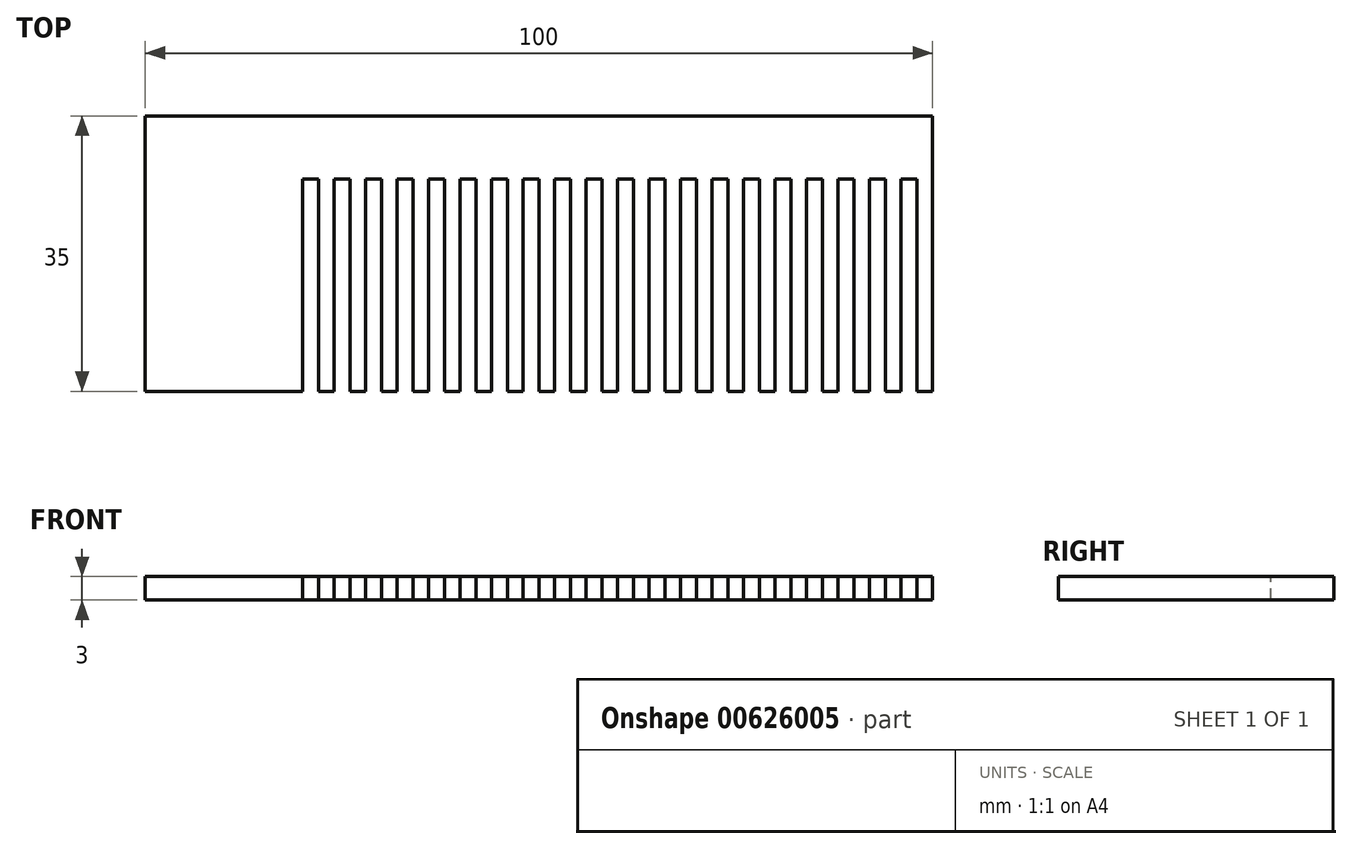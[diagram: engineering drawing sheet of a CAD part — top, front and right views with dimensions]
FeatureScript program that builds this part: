
annotation { "Feature Type Name" : "Feature", "Feature Type Description" : "" }
export const myFeature = defineFeature(function(context is Context, id is Id, definition is map)
    precondition{}
    {
        {
            var Q0;
            Q0=qCreatedBy(makeId("Top.planeOp"),FACE);
            var sketch = newSketch(context, id + "F0", { "sketchPlane" : qUnion([Q0])});
            skLineSegment(sketch, "E0.bottom", {"start": v(-50, 17.5) * mm, "end": v(50, 17.5) * mm});
            skLineSegment(sketch, "E0.top", {"start": v(-50, -17.5) * mm, "end": v(50, -17.5) * mm});
            skLineSegment(sketch, "E0.left", {"start": v(-50, 17.5) * mm, "end": v(-50, -17.5) * mm});
            skLineSegment(sketch, "E0.right", {"start": v(50, 17.5) * mm, "end": v(50, -17.5) * mm});
            skPoint(sketch, "E0.middle", {"position": v(0, 0) * mm});
            skSolve(sketch);
        }
        {
            var Q0;
            Q0=makeQuery(id+"F0.imprint","IMPRINT",FACE,{"disambiguationData":[TD([[makeQuery(id+"F0.imprint","IMPRINT",EDGE,{"derivedFrom":sQuery(id+"F0.wireOp",EDGE,"E0.bottom")}),-1.0]])]});
            extrude(context, id + "F1", {"entities" : qUnion([Q0]), "depth" : 3 * mm, "offsetDistance" : 25.4 * mm});
        }
        {
            var Q0;
            Q0=makeQuery(id+"F1.opExtrude","CAP_FACE",FACE,{"disambiguationData":[OSD([sQuery(id+"F0.wireOp",EDGE,"E0.bottom"),sQuery(id+"F0.wireOp",EDGE,"E0.top"),sQuery(id+"F0.wireOp",EDGE,"E0.left"),sQuery(id+"F0.wireOp",EDGE,"E0.right")])],"isStart":false});
            var sketch = newSketch(context, id + "F2", { "sketchPlane" : qUnion([Q0])});
            skLineSegment(sketch, "E1.bottom", {"start": v(46, 9.5) * mm, "end": v(48, 9.5) * mm});
            skLineSegment(sketch, "E1.top", {"start": v(46, -25.5) * mm, "end": v(48, -25.5) * mm});
            skLineSegment(sketch, "E1.left", {"start": v(46, 9.5) * mm, "end": v(46, -25.5) * mm});
            skLineSegment(sketch, "E1.right", {"start": v(48, 9.5) * mm, "end": v(48, -25.5) * mm});
            skLineSegment(sketch, "E2.1.0.0", {"start": v(42, 9.5) * mm, "end": v(44, 9.5) * mm});
            skLineSegment(sketch, "E2.1.0.1", {"start": v(42, -25.5) * mm, "end": v(44, -25.5) * mm});
            skLineSegment(sketch, "E2.1.0.2", {"start": v(42, 9.5) * mm, "end": v(42, -25.5) * mm});
            skLineSegment(sketch, "E2.1.0.3", {"start": v(44, 9.5) * mm, "end": v(44, -25.5) * mm});
            skLineSegment(sketch, "E2.2.0.0", {"start": v(38, 9.5) * mm, "end": v(40, 9.5) * mm});
            skLineSegment(sketch, "E2.2.0.1", {"start": v(38, -25.5) * mm, "end": v(40, -25.5) * mm});
            skLineSegment(sketch, "E2.2.0.2", {"start": v(38, 9.5) * mm, "end": v(38, -25.5) * mm});
            skLineSegment(sketch, "E2.2.0.3", {"start": v(40, 9.5) * mm, "end": v(40, -25.5) * mm});
            skLineSegment(sketch, "E2.3.0.0", {"start": v(34, 9.5) * mm, "end": v(36, 9.5) * mm});
            skLineSegment(sketch, "E2.3.0.1", {"start": v(34, -25.5) * mm, "end": v(36, -25.5) * mm});
            skLineSegment(sketch, "E2.3.0.2", {"start": v(34, 9.5) * mm, "end": v(34, -25.5) * mm});
            skLineSegment(sketch, "E2.3.0.3", {"start": v(36, 9.5) * mm, "end": v(36, -25.5) * mm});
            skLineSegment(sketch, "E2.4.0.0", {"start": v(30, 9.5) * mm, "end": v(32, 9.5) * mm});
            skLineSegment(sketch, "E2.4.0.1", {"start": v(30, -25.5) * mm, "end": v(32, -25.5) * mm});
            skLineSegment(sketch, "E2.4.0.2", {"start": v(30, 9.5) * mm, "end": v(30, -25.5) * mm});
            skLineSegment(sketch, "E2.4.0.3", {"start": v(32, 9.5) * mm, "end": v(32, -25.5) * mm});
            skLineSegment(sketch, "E2.5.0.0", {"start": v(26, 9.5) * mm, "end": v(28, 9.5) * mm});
            skLineSegment(sketch, "E2.5.0.1", {"start": v(26, -25.5) * mm, "end": v(28, -25.5) * mm});
            skLineSegment(sketch, "E2.5.0.2", {"start": v(26, 9.5) * mm, "end": v(26, -25.5) * mm});
            skLineSegment(sketch, "E2.5.0.3", {"start": v(28, 9.5) * mm, "end": v(28, -25.5) * mm});
            skLineSegment(sketch, "E2.6.0.0", {"start": v(22, 9.5) * mm, "end": v(24, 9.5) * mm});
            skLineSegment(sketch, "E2.6.0.1", {"start": v(22, -25.5) * mm, "end": v(24, -25.5) * mm});
            skLineSegment(sketch, "E2.6.0.2", {"start": v(22, 9.5) * mm, "end": v(22, -25.5) * mm});
            skLineSegment(sketch, "E2.6.0.3", {"start": v(24, 9.5) * mm, "end": v(24, -25.5) * mm});
            skLineSegment(sketch, "E2.7.0.0", {"start": v(18, 9.5) * mm, "end": v(20, 9.5) * mm});
            skLineSegment(sketch, "E2.7.0.1", {"start": v(18, -25.5) * mm, "end": v(20, -25.5) * mm});
            skLineSegment(sketch, "E2.7.0.2", {"start": v(18, 9.5) * mm, "end": v(18, -25.5) * mm});
            skLineSegment(sketch, "E2.7.0.3", {"start": v(20, 9.5) * mm, "end": v(20, -25.5) * mm});
            skLineSegment(sketch, "E2.8.0.0", {"start": v(14, 9.5) * mm, "end": v(16, 9.5) * mm});
            skLineSegment(sketch, "E2.8.0.1", {"start": v(14, -25.5) * mm, "end": v(16, -25.5) * mm});
            skLineSegment(sketch, "E2.8.0.2", {"start": v(14, 9.5) * mm, "end": v(14, -25.5) * mm});
            skLineSegment(sketch, "E2.8.0.3", {"start": v(16, 9.5) * mm, "end": v(16, -25.5) * mm});
            skLineSegment(sketch, "E2.9.0.0", {"start": v(10, 9.5) * mm, "end": v(12, 9.5) * mm});
            skLineSegment(sketch, "E2.9.0.1", {"start": v(10, -25.5) * mm, "end": v(12, -25.5) * mm});
            skLineSegment(sketch, "E2.9.0.2", {"start": v(10, 9.5) * mm, "end": v(10, -25.5) * mm});
            skLineSegment(sketch, "E2.9.0.3", {"start": v(12, 9.5) * mm, "end": v(12, -25.5) * mm});
            skLineSegment(sketch, "E2.10.0.0", {"start": v(6, 9.5) * mm, "end": v(8, 9.5) * mm});
            skLineSegment(sketch, "E2.10.0.1", {"start": v(6, -25.5) * mm, "end": v(8, -25.5) * mm});
            skLineSegment(sketch, "E2.10.0.2", {"start": v(6, 9.5) * mm, "end": v(6, -25.5) * mm});
            skLineSegment(sketch, "E2.10.0.3", {"start": v(8, 9.5) * mm, "end": v(8, -25.5) * mm});
            skLineSegment(sketch, "E2.11.0.0", {"start": v(2, 9.5) * mm, "end": v(4, 9.5) * mm});
            skLineSegment(sketch, "E2.11.0.1", {"start": v(2, -25.5) * mm, "end": v(4, -25.5) * mm});
            skLineSegment(sketch, "E2.11.0.2", {"start": v(2, 9.5) * mm, "end": v(2, -25.5) * mm});
            skLineSegment(sketch, "E2.11.0.3", {"start": v(4, 9.5) * mm, "end": v(4, -25.5) * mm});
            skLineSegment(sketch, "E2.12.0.0", {"start": v(-2, 9.5) * mm, "end": v(0, 9.5) * mm});
            skLineSegment(sketch, "E2.12.0.1", {"start": v(-2, -25.5) * mm, "end": v(0, -25.5) * mm});
            skLineSegment(sketch, "E2.12.0.2", {"start": v(-2, 9.5) * mm, "end": v(-2, -25.5) * mm});
            skLineSegment(sketch, "E2.12.0.3", {"start": v(0, 9.5) * mm, "end": v(0, -25.5) * mm});
            skLineSegment(sketch, "E2.13.0.0", {"start": v(-6, 9.5) * mm, "end": v(-4, 9.5) * mm});
            skLineSegment(sketch, "E2.13.0.1", {"start": v(-6, -25.5) * mm, "end": v(-4, -25.5) * mm});
            skLineSegment(sketch, "E2.13.0.2", {"start": v(-6, 9.5) * mm, "end": v(-6, -25.5) * mm});
            skLineSegment(sketch, "E2.13.0.3", {"start": v(-4, 9.5) * mm, "end": v(-4, -25.5) * mm});
            skLineSegment(sketch, "E2.14.0.0", {"start": v(-10, 9.5) * mm, "end": v(-8, 9.5) * mm});
            skLineSegment(sketch, "E2.14.0.1", {"start": v(-10, -25.5) * mm, "end": v(-8, -25.5) * mm});
            skLineSegment(sketch, "E2.14.0.2", {"start": v(-10, 9.5) * mm, "end": v(-10, -25.5) * mm});
            skLineSegment(sketch, "E2.14.0.3", {"start": v(-8, 9.5) * mm, "end": v(-8, -25.5) * mm});
            skLineSegment(sketch, "E2.15.0.0", {"start": v(-14, 9.5) * mm, "end": v(-12, 9.5) * mm});
            skLineSegment(sketch, "E2.15.0.1", {"start": v(-14, -25.5) * mm, "end": v(-12, -25.5) * mm});
            skLineSegment(sketch, "E2.15.0.2", {"start": v(-14, 9.5) * mm, "end": v(-14, -25.5) * mm});
            skLineSegment(sketch, "E2.15.0.3", {"start": v(-12, 9.5) * mm, "end": v(-12, -25.5) * mm});
            skLineSegment(sketch, "E2.16.0.0", {"start": v(-18, 9.5) * mm, "end": v(-16, 9.5) * mm});
            skLineSegment(sketch, "E2.16.0.1", {"start": v(-18, -25.5) * mm, "end": v(-16, -25.5) * mm});
            skLineSegment(sketch, "E2.16.0.2", {"start": v(-18, 9.5) * mm, "end": v(-18, -25.5) * mm});
            skLineSegment(sketch, "E2.16.0.3", {"start": v(-16, 9.5) * mm, "end": v(-16, -25.5) * mm});
            skLineSegment(sketch, "E2.17.0.0", {"start": v(-22, 9.5) * mm, "end": v(-20, 9.5) * mm});
            skLineSegment(sketch, "E2.17.0.1", {"start": v(-22, -25.5) * mm, "end": v(-20, -25.5) * mm});
            skLineSegment(sketch, "E2.17.0.2", {"start": v(-22, 9.5) * mm, "end": v(-22, -25.5) * mm});
            skLineSegment(sketch, "E2.17.0.3", {"start": v(-20, 9.5) * mm, "end": v(-20, -25.5) * mm});
            skLineSegment(sketch, "E2.18.0.0", {"start": v(-26, 9.5) * mm, "end": v(-24, 9.5) * mm});
            skLineSegment(sketch, "E2.18.0.1", {"start": v(-26, -25.5) * mm, "end": v(-24, -25.5) * mm});
            skLineSegment(sketch, "E2.18.0.2", {"start": v(-26, 9.5) * mm, "end": v(-26, -25.5) * mm});
            skLineSegment(sketch, "E2.18.0.3", {"start": v(-24, 9.5) * mm, "end": v(-24, -25.5) * mm});
            skLineSegment(sketch, "E2.19.0.0", {"start": v(-30, 9.5) * mm, "end": v(-28, 9.5) * mm});
            skLineSegment(sketch, "E2.19.0.1", {"start": v(-30, -25.5) * mm, "end": v(-28, -25.5) * mm});
            skLineSegment(sketch, "E2.19.0.2", {"start": v(-30, 9.5) * mm, "end": v(-30, -25.5) * mm});
            skLineSegment(sketch, "E2.19.0.3", {"start": v(-28, 9.5) * mm, "end": v(-28, -25.5) * mm});
            skLineSegment(sketch, "E2.direction1", {"start": v(46, -25.5) * mm, "end": v(42, -25.5) * mm, "construction": true});
            skSolve(sketch);
        }
        {
            var Q0;
            Q0 = qSketchRegion(id + "F2", true);
            extrude(context, id + "F3", {"entities" : qUnion([Q0]), "operationType" : NewBodyOperationType.REMOVE, "endBound" : BoundingType.THROUGH_ALL, "oppositeDirection" : true, "depth" : 25.4 * mm, "offsetDistance" : 25.4 * mm});
        }
    });
